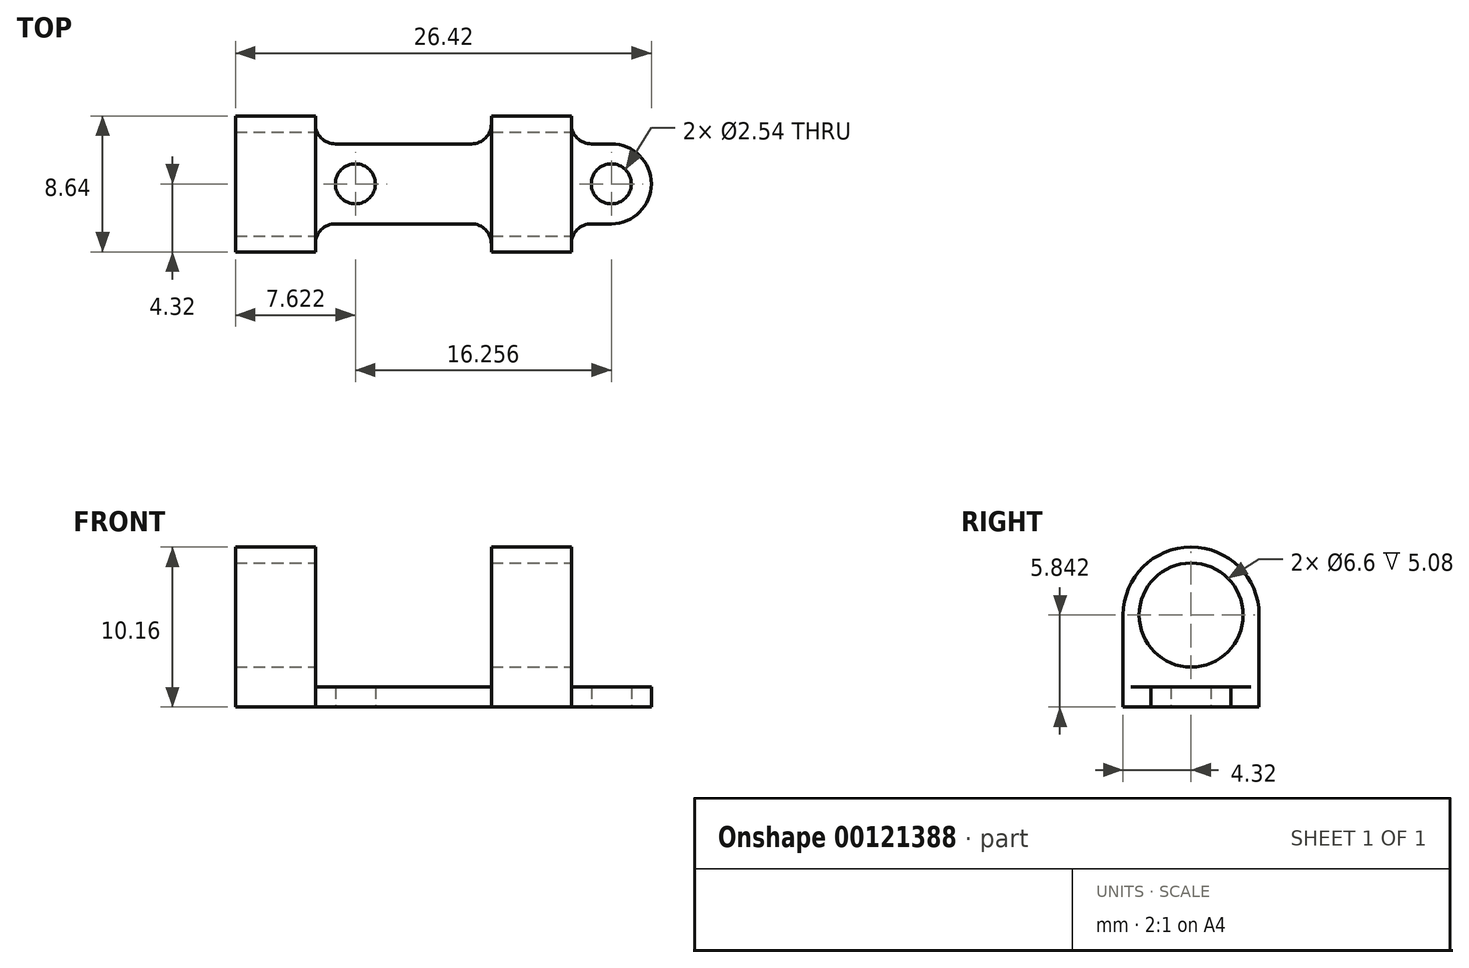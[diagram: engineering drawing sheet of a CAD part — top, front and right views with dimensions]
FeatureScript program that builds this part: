
annotation { "Feature Type Name" : "Feature", "Feature Type Description" : "" }
export const myFeature = defineFeature(function(context is Context, id is Id, definition is map)
    precondition{}
    {
        {
            var Q0;
            Q0=qCreatedBy(makeId("Top.planeOp"),FACE);
            var sketch = newSketch(context, id + "F0", { "sketchPlane" : qUnion([Q0])});
            skCircle(sketch, "E0", {"center": v(-8.13, 0) * mm, "radius": 1.27 * mm});
            skCircle(sketch, "E1", {"center": v(8.13, 0) * mm, "radius": 1.27 * mm});
            skLineSegment(sketch, "E2", {"start": v(-8.13, 0) * mm, "end": v(8.13, 0) * mm, "construction": true});
            skPoint(sketch, "E3", {"position": v(0, 0) * mm});
            skCircle(sketch, "E4", {"center": v(-8.13, 0) * mm, "radius": 2.54 * mm, "construction": true});
            skCircle(sketch, "E5", {"center": v(8.13, 0) * mm, "radius": 2.54 * mm, "construction": true});
            skLineSegment(sketch, "E6", {"start": v(-15.75, 5.71) * mm, "end": v(-15.75, -5.72) * mm});
            skLineSegment(sketch, "E7", {"start": v(-15.75, -5.72) * mm, "end": v(-10.67, -5.72) * mm});
            skLineSegment(sketch, "E8", {"start": v(-10.67, -5.72) * mm, "end": v(-10.67, -2.54) * mm});
            skLineSegment(sketch, "E9", {"start": v(-10.67, -2.54) * mm, "end": v(0.5, -2.54) * mm});
            skLineSegment(sketch, "E10", {"start": v(0.5, -2.54) * mm, "end": v(0.5, -5.72) * mm});
            skLineSegment(sketch, "E11", {"start": v(0.5, -5.72) * mm, "end": v(5.59, -5.72) * mm});
            skLineSegment(sketch, "E12", {"start": v(5.59, -5.72) * mm, "end": v(5.59, -2.54) * mm});
            skLineSegment(sketch, "E13", {"start": v(-15.75, 5.71) * mm, "end": v(-10.67, 5.71) * mm});
            skLineSegment(sketch, "E14", {"start": v(-10.67, 5.71) * mm, "end": v(-10.67, 2.54) * mm});
            skLineSegment(sketch, "E15", {"start": v(-10.67, 2.54) * mm, "end": v(0.5, 2.54) * mm});
            skLineSegment(sketch, "E16", {"start": v(0.5, 2.54) * mm, "end": v(0.5, 5.71) * mm});
            skLineSegment(sketch, "E17", {"start": v(0.5, 5.71) * mm, "end": v(5.59, 5.71) * mm});
            skLineSegment(sketch, "E18", {"start": v(5.59, 5.71) * mm, "end": v(5.59, 2.54) * mm});
            skLineSegment(sketch, "E19", {"start": v(5.59, 2.54) * mm, "end": v(8.13, 2.54) * mm});
            skLineSegment(sketch, "E20", {"start": v(5.59, -2.54) * mm, "end": v(8.13, -2.54) * mm});
            skArc(sketch, "E21", {"start": v(8.13, -2.54) * mm, "mid": v(10.67, 0) * mm, "end": v(8.13, 2.54) * mm});
            skLineSegment(sketch, "E22", {"start": v(0.5, 2.54) * mm, "end": v(0.5, -2.54) * mm, "construction": true});
            skSolve(sketch);
        }
        {
            var Q0;
            Q0 = qSketchRegion(id + "F0", true);
            extrude(context, id + "F1", {"entities" : qUnion([Q0]), "depth" : 1.27 * mm});
        }
        {
            var Q0;
            Q0=makeQuery(id+"F1.opExtrude","CAP_FACE",FACE,{"disambiguationData":[OSD([sQuery(id+"F0.wireOp",EDGE,"E0"),sQuery(id+"F0.wireOp",EDGE,"E1"),sQuery(id+"F0.wireOp",EDGE,"E6"),sQuery(id+"F0.wireOp",EDGE,"E7"),sQuery(id+"F0.wireOp",EDGE,"E8"),sQuery(id+"F0.wireOp",EDGE,"E9"),sQuery(id+"F0.wireOp",EDGE,"E10"),sQuery(id+"F0.wireOp",EDGE,"E11"),sQuery(id+"F0.wireOp",EDGE,"E12"),sQuery(id+"F0.wireOp",EDGE,"E13"),sQuery(id+"F0.wireOp",EDGE,"E14"),sQuery(id+"F0.wireOp",EDGE,"E15"),sQuery(id+"F0.wireOp",EDGE,"E16"),sQuery(id+"F0.wireOp",EDGE,"E17"),sQuery(id+"F0.wireOp",EDGE,"E18"),sQuery(id+"F0.wireOp",EDGE,"E19"),sQuery(id+"F0.wireOp",EDGE,"E20"),sQuery(id+"F0.wireOp",EDGE,"E21")])],"isStart":false});
            var sketch = newSketch(context, id + "F2", { "sketchPlane" : qUnion([Q0])});
            skLineSegment(sketch, "E23.bottom", {"start": v(-15.75, 5.71) * mm, "end": v(-10.67, 5.71) * mm});
            skLineSegment(sketch, "E23.top", {"start": v(-15.75, -5.72) * mm, "end": v(-10.67, -5.72) * mm});
            skLineSegment(sketch, "E23.left", {"start": v(-15.75, 5.71) * mm, "end": v(-15.75, -5.71) * mm});
            skLineSegment(sketch, "E23.right", {"start": v(-10.67, 5.71) * mm, "end": v(-10.67, -5.71) * mm});
            skLineSegment(sketch, "E24.bottom", {"start": v(0.5, -5.72) * mm, "end": v(5.59, -5.72) * mm});
            skLineSegment(sketch, "E24.top", {"start": v(0.5, 5.71) * mm, "end": v(5.59, 5.71) * mm});
            skLineSegment(sketch, "E24.left", {"start": v(0.5, -5.72) * mm, "end": v(0.5, 5.71) * mm});
            skLineSegment(sketch, "E24.right", {"start": v(5.59, -5.72) * mm, "end": v(5.59, 5.71) * mm});
            skSolve(sketch);
        }
        {
            var Q0;
            Q0 = qSketchRegion(id + "F2", true);
            extrude(context, id + "F3", {"entities" : qUnion([Q0]), "operationType" : NewBodyOperationType.ADD, "depth" : 8.9 * mm});
        }
        {
            var Q0;
            Q0=makeQuery(id+"F3.boolean.opBoolean","MERGE",FACE,{"derivedFrom":[makeQuery(id+"F1.opExtrude","SWEPT_FACE",FACE,{"disambiguationData":[OSD([sQuery(id+"F0.wireOp",EDGE,"E12")])]}),makeQuery(id+"F1.opExtrude","SWEPT_FACE",FACE,{"disambiguationData":[OSD([sQuery(id+"F0.wireOp",EDGE,"E18")])]}),makeQuery(id+"F3.opExtrude","SWEPT_FACE",FACE,{"disambiguationData":[OSD([sQuery(id+"F2.wireOp",EDGE,"E24.right")])]})]});
            var sketch = newSketch(context, id + "F4", { "sketchPlane" : qUnion([Q0])});
            skCircle(sketch, "E25", {"center": v(0, 5.84) * mm, "radius": 3.3 * mm});
            skLineSegment(sketch, "E26", {"start": v(-4.32, 0) * mm, "end": v(-5.72, 0) * mm});
            skLineSegment(sketch, "E27", {"start": v(-5.72, 0) * mm, "end": v(-5.72, 10.16) * mm});
            skLineSegment(sketch, "E28", {"start": v(-5.72, 10.16) * mm, "end": v(5.71, 10.16) * mm});
            skLineSegment(sketch, "E29", {"start": v(5.71, 10.16) * mm, "end": v(5.72, 0) * mm});
            skLineSegment(sketch, "E30", {"start": v(5.71, 0) * mm, "end": v(4.32, 0) * mm});
            skLineSegment(sketch, "E31", {"start": v(4.32, 0) * mm, "end": v(4.32, 5.84) * mm});
            skLineSegment(sketch, "E32", {"start": v(-4.32, 0) * mm, "end": v(-4.32, 5.84) * mm});
            skArc(sketch, "E33", {"start": v(4.32, 5.84) * mm, "mid": v(0, 10.16) * mm, "end": v(-4.32, 5.84) * mm});
            skSolve(sketch);
        }
        {
            var Q0;
            Q0 = qSketchRegion(id + "F4", true);
            var Q1;
            Q1=makeQuery(id+"F3.boolean.opBoolean","MERGE",FACE,{"derivedFrom":[makeQuery(id+"F1.opExtrude","SWEPT_FACE",FACE,{"disambiguationData":[OSD([sQuery(id+"F0.wireOp",EDGE,"E6")])]}),makeQuery(id+"F3.opExtrude","SWEPT_FACE",FACE,{"disambiguationData":[OSD([sQuery(id+"F2.wireOp",EDGE,"E23.left")])]})]});
            extrude(context, id + "F5", {"entities" : qUnion([Q0]), "operationType" : NewBodyOperationType.REMOVE, "endBound" : BoundingType.UP_TO_SURFACE, "oppositeDirection" : true, "endBoundEntityFace" : qUnion([Q1]), "depth" : 25.4 * mm});
        }
        {
            var Q0;
            Q0=makeQuery(id+"F1.opExtrude","SWEPT_EDGE",EDGE,{"disambiguationData":[OSD([sQuery(id+"F0.wireOp",EDGE,"E8"),sQuery(id+"F0.wireOp",EDGE,"E9")])]});
            var Q1;
            Q1=makeQuery(id+"F1.opExtrude","SWEPT_EDGE",EDGE,{"disambiguationData":[OSD([sQuery(id+"F0.wireOp",EDGE,"E12"),sQuery(id+"F0.wireOp",EDGE,"E20")])]});
            var Q2;
            Q2=makeQuery(id+"F1.opExtrude","SWEPT_EDGE",EDGE,{"disambiguationData":[OSD([sQuery(id+"F0.wireOp",EDGE,"E9"),sQuery(id+"F0.wireOp",EDGE,"E10")])]});
            var Q3;
            Q3=makeQuery(id+"F1.opExtrude","SWEPT_EDGE",EDGE,{"disambiguationData":[OSD([sQuery(id+"F0.wireOp",EDGE,"E15"),sQuery(id+"F0.wireOp",EDGE,"E16")])]});
            var Q4;
            Q4=makeQuery(id+"F1.opExtrude","SWEPT_EDGE",EDGE,{"disambiguationData":[OSD([sQuery(id+"F0.wireOp",EDGE,"E18"),sQuery(id+"F0.wireOp",EDGE,"E19")])]});
            var Q5;
            Q5=makeQuery(id+"F1.opExtrude","SWEPT_EDGE",EDGE,{"disambiguationData":[OSD([sQuery(id+"F0.wireOp",EDGE,"E14"),sQuery(id+"F0.wireOp",EDGE,"E15")])]});
            fillet(context, id + "F6", {"entities" : qUnion([Q0, Q1, Q2, Q3, Q4, Q5]), "radius" : 1.27 * mm, "tangentPropagation" : true, "allowEdgeOverflow" : false});
        }
    });
